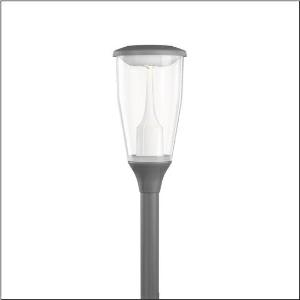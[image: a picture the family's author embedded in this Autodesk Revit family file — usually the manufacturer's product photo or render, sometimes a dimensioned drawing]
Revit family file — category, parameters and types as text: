
# Revit family: dl_11_iq___st1_2a_5xa5565kf14h000022_1156
name_source: partatom
category: Lighting Fixtures
units: mm (PartAtom-declared; Revit-internal decimal feet)

## family parameters
Cut with Voids When Loaded = No
Host = Face
Light Source = No
Part Type = Normal
Room Calculation Point = No
Round Connector Dimension = Use Diameter
Shared = No

## types (1)
- --- (1 x LED, 1560 lm, 10 W, 4000K)
    Apparent Load = 10 VA
    CIE Flux Codes = 24 63 94 96 100
    Color Rendering = 70
    Color Temperature = 4000K
    Default Elevation = 1800 mm
    Description = DL 11 iQ, mast luminaire, Module 540 iQ-SR, primary light control with 3 zone facetted reflector, of plastic, silver coated, highly specular, structured, primary optical cover: cover, of PMMA, transparent, light distribution: ST1.2a, light emission: direct distribution, primary light characteristic: asymmetric, installation type: post-top, LED, High Power LED, rated luminous flux: 1.560lm, luminous efficacy: 149lm/W, light colour: 740, colour temperature: 4000K, control: Street-Remote, Auto-Match, Temp-Guard, Lumen-Switch, Night-Set, Smart-Wire, Light-Fading, Desk-Remote (wireless, voltage-free reading and setting of iQ features in the workshop via application-optimized NFC function/RFID function), optimised constant luminous flux control (CLO 2.0), mains connection: 220..240V, AC, 50/60Hz, connection cable pre-assembled, cable length: 5,5m, start of lifetime: 10W, end of service life: 10W, reduction: 5W, luminaire housing, upper part, of diecast aluminium, coated, Siteco® metallic grey (DB 702S), spigot size: 60mm (post-top), post-top mast mounting element, of diecast aluminium, coated, Siteco® metallic grey (DB 702S), Module 540 iQ-SR, traffic white (RAL 9016), equipment: standard, protection rating (complete): IP66, insulation class (complete): insulation class II (safety insulation), certification: CE, ENEC, ENEC+, VDE, packaging unit: 1 piece

Light Distribution: ST1.2a
    Height = 665 mm
    Lamp = 1 x LED
    Lamp Light Flux = 1560 lm
    Lamp Power = 10 W
    Lamp count = 1
    Length = 334 mm
    Luminous efficacy = 156 lm/W
    Manufacturer = Siteco
    ModVariant = No
    Model = 5XA5565KF14H000022
    Number of Poles = 1
    OnlyDefault = Yes
    Power Factor = 1
    Product Name = DL 11 iQ | ST1.2a
    Product group = mast luminaire | pylon top
    ProductGroupID = 6100
    Protection Class = Protection class II
    Protection Degree = IP 66
    RLX_Detail_Level = 1
    RLX_Emergency_Light_Flux = 0 lm
    RLX_Emergency_Type = 0
    RLX_Emergency_Type_DB = No
    RlxData = <blob elided: 157433 chars, md5=1b523bc6>
    Socket = socket
    Standby Power = 0 W
    System Light Flux = 1560 lm
    System Power = 10 W
    Type Comments = factory setting: luminous flux: 100 % | dim-lin: 254 | 401 mA
    Type Image = l_1258354.jpg
    URL = http://relux.com
    VarID = @adj_025871
    Voltage = 0 V
    Weight = 0.00 kg
    Width = 0 mm  [stored 0 ft]

note: [stored X ft] marks values corroborated as IEEE doubles in the binary element streams (Revit-internal decimal feet)

## geometry (parser evidence)
native form markers: Blend x4, Sweep x11
no freeform markers — native parametric forms only
